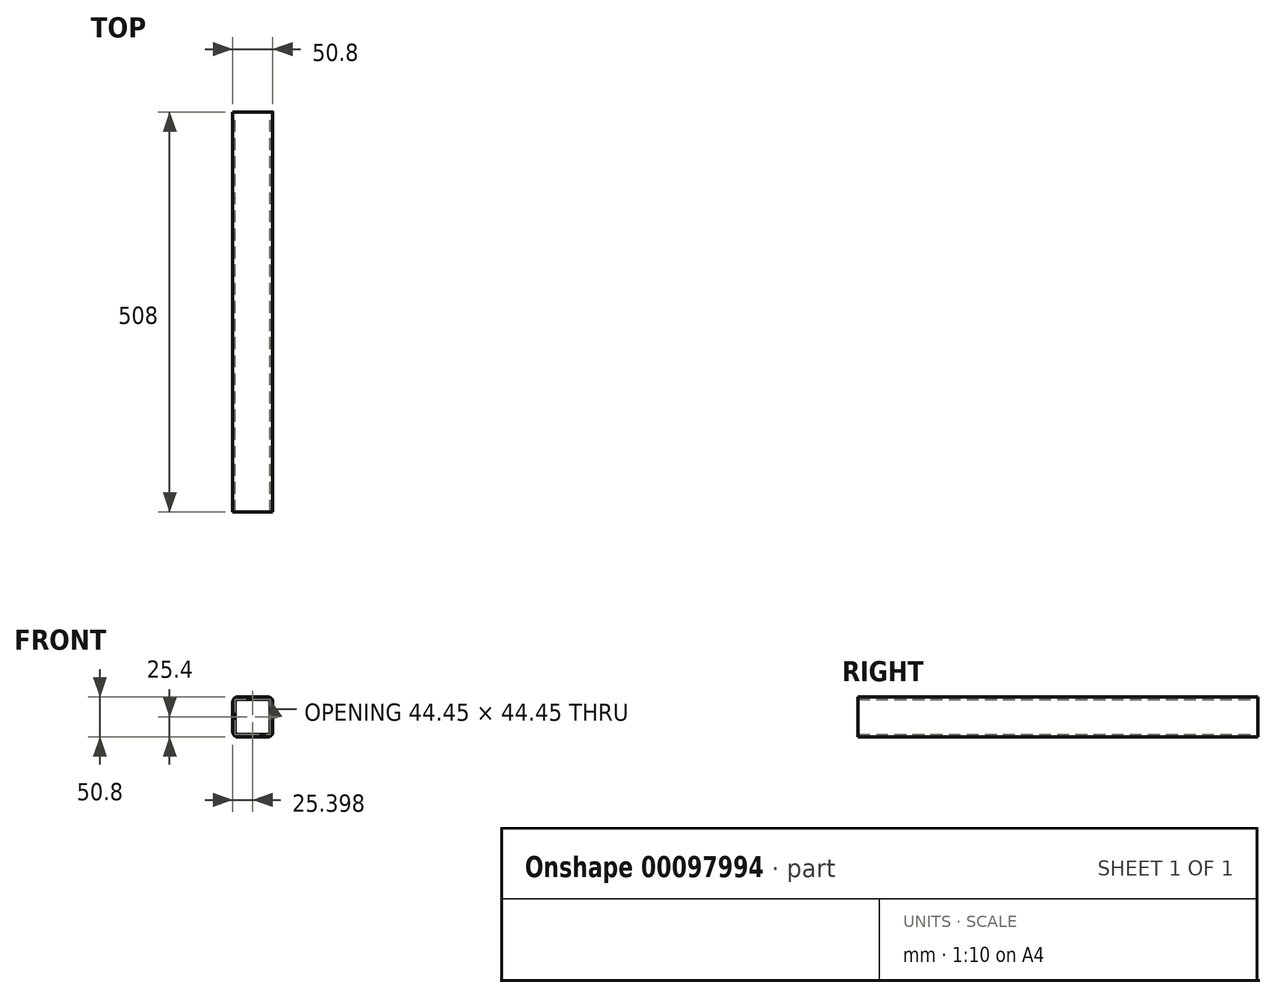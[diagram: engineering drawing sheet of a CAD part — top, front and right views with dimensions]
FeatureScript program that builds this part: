
annotation { "Feature Type Name" : "Feature", "Feature Type Description" : "" }
export const myFeature = defineFeature(function(context is Context, id is Id, definition is map)
    precondition{}
    {
        {
            var Q0;
            Q0=qCreatedBy(makeId("Front.planeOp"),FACE);
            var sketch = newSketch(context, id + "F0", { "sketchPlane" : qUnion([Q0])});
            skLineSegment(sketch, "E0.bottom", {"start": v(18.9, -25.4) * mm, "end": v(-19.2, -25.4) * mm});
            skLineSegment(sketch, "E0.top", {"start": v(18.9, 25.4) * mm, "end": v(-19.2, 25.4) * mm});
            skLineSegment(sketch, "E0.left", {"start": v(25.26, -19.05) * mm, "end": v(25.26, 19.05) * mm});
            skLineSegment(sketch, "E0.right", {"start": v(-25.54, -19.05) * mm, "end": v(-25.54, 19.05) * mm});
            skPoint(sketch, "E0.middle", {"position": v(-0.14, 0) * mm});
            skLineSegment(sketch, "E1.bottom", {"start": v(18.9, 22.22) * mm, "end": v(-19.2, 22.22) * mm});
            skLineSegment(sketch, "E1.top", {"start": v(18.9, -22.23) * mm, "end": v(-19.2, -22.23) * mm});
            skLineSegment(sketch, "E1.left", {"start": v(22.08, 19.05) * mm, "end": v(22.08, -19.05) * mm});
            skLineSegment(sketch, "E1.right", {"start": v(-22.37, 19.05) * mm, "end": v(-22.37, -19.05) * mm});
            skPoint(sketch, "E2.visualSharp", {"position": v(-25.54, 25.4) * mm});
            skArc(sketch, "E2.filletArc", {"start": v(-19.2, 25.4) * mm, "mid": v(-23.68, 23.54) * mm, "end": v(-25.54, 19.05) * mm});
            skPoint(sketch, "E3.visualSharp", {"position": v(25.26, 25.4) * mm});
            skArc(sketch, "E3.filletArc", {"start": v(25.26, 19.05) * mm, "mid": v(23.4, 23.54) * mm, "end": v(18.9, 25.4) * mm});
            skPoint(sketch, "E4.visualSharp", {"position": v(25.26, -25.4) * mm});
            skArc(sketch, "E4.filletArc", {"start": v(18.9, -25.4) * mm, "mid": v(23.4, -23.54) * mm, "end": v(25.26, -19.05) * mm});
            skPoint(sketch, "E5.visualSharp", {"position": v(-25.54, -25.4) * mm});
            skArc(sketch, "E5.filletArc", {"start": v(-25.54, -19.05) * mm, "mid": v(-23.68, -23.54) * mm, "end": v(-19.2, -25.4) * mm});
            skPoint(sketch, "E6.visualSharp", {"position": v(22.08, 22.22) * mm});
            skArc(sketch, "E6.filletArc", {"start": v(22.08, 19.05) * mm, "mid": v(21.15, 21.3) * mm, "end": v(18.9, 22.22) * mm});
            skPoint(sketch, "E7.visualSharp", {"position": v(22.08, -22.23) * mm});
            skArc(sketch, "E7.filletArc", {"start": v(18.9, -22.23) * mm, "mid": v(21.15, -21.3) * mm, "end": v(22.08, -19.05) * mm});
            skPoint(sketch, "E8.visualSharp", {"position": v(-22.37, -22.23) * mm});
            skArc(sketch, "E8.filletArc", {"start": v(-22.37, -19.05) * mm, "mid": v(-21.44, -21.3) * mm, "end": v(-19.2, -22.23) * mm});
            skPoint(sketch, "E9.visualSharp", {"position": v(-22.37, 22.22) * mm});
            skArc(sketch, "E9.filletArc", {"start": v(-19.2, 22.22) * mm, "mid": v(-21.44, 21.3) * mm, "end": v(-22.37, 19.05) * mm});
            skSolve(sketch);
        }
        {
            var Q0;
            Q0=makeQuery(id+"F0.imprint","IMPRINT",FACE,{"disambiguationData":[TD([[makeQuery(id+"F0.imprint","IMPRINT",EDGE,{"derivedFrom":sQuery(id+"F0.wireOp",EDGE,"E0.bottom")}),-1.0]])]});
            extrude(context, id + "F1", {"entities" : qUnion([Q0]), "endBound" : BoundingType.SYMMETRIC, "depth" : 508 * mm});
        }
    });
